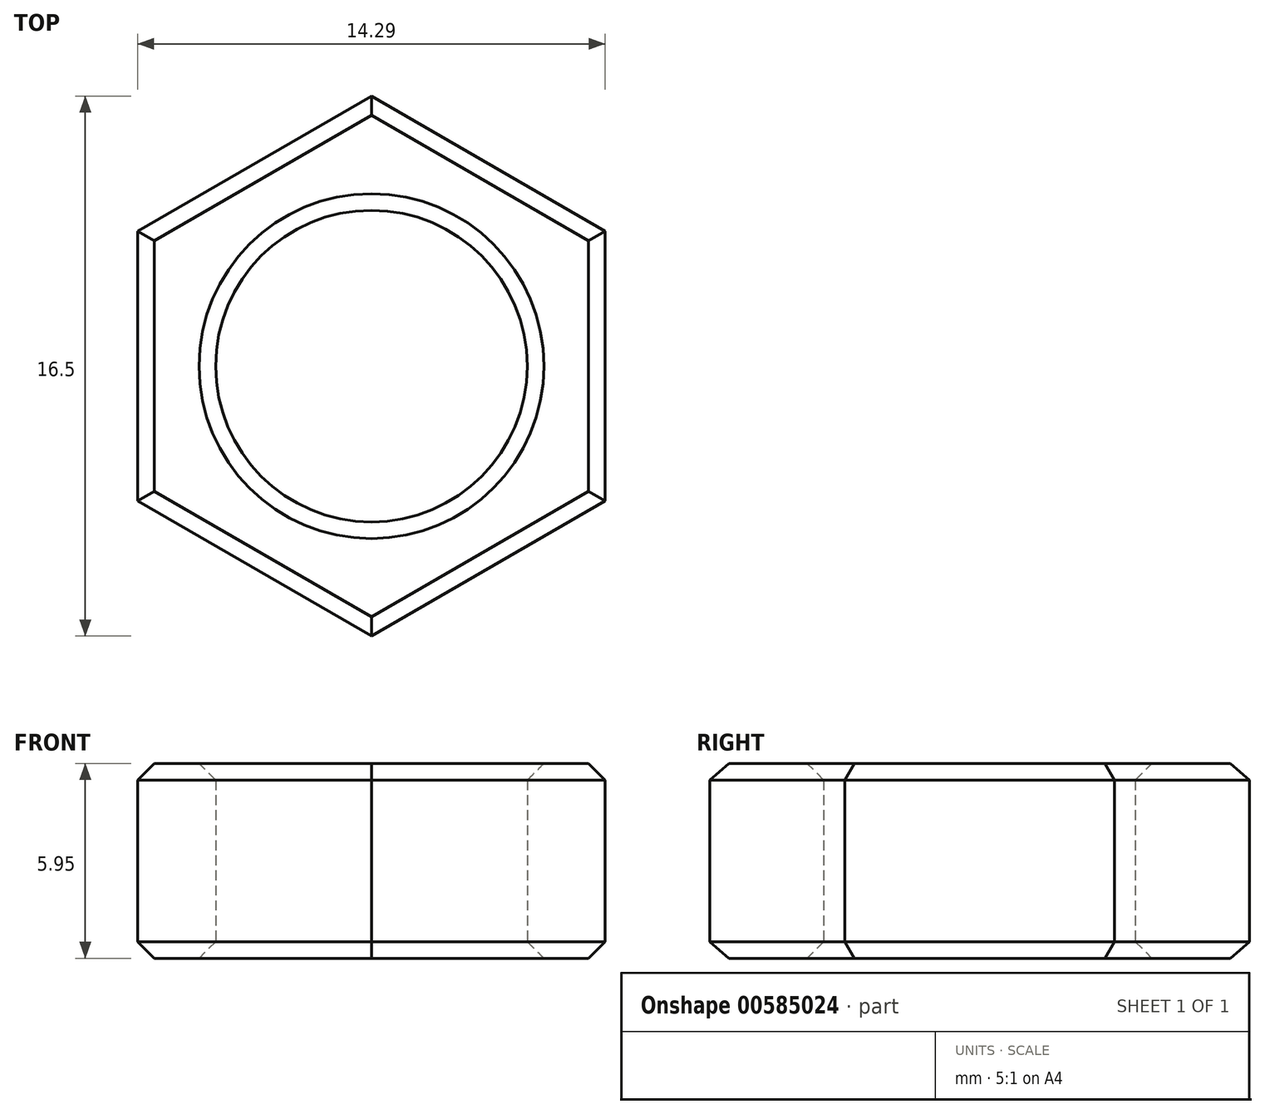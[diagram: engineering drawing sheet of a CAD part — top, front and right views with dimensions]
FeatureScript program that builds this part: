
annotation { "Feature Type Name" : "Feature", "Feature Type Description" : "" }
export const myFeature = defineFeature(function(context is Context, id is Id, definition is map)
    precondition{}
    {
        {
            var Q0;
            Q0=qCreatedBy(makeId("Top.planeOp"),FACE);
            var sketch = newSketch(context, id + "F0", { "sketchPlane" : qUnion([Q0])});
            skCircle(sketch, "E0.cCircle", {"center": v(-0.14, 0.22) * mm, "radius": 7.14 * mm, "construction": true});
            skLineSegment(sketch, "E0.0", {"start": v(7, 4.34) * mm, "end": v(7, -3.9) * mm});
            skLineSegment(sketch, "E0.1", {"start": v(7, -3.9) * mm, "end": v(-0.14, -8.03) * mm});
            skLineSegment(sketch, "E0.2", {"start": v(-0.14, -8.03) * mm, "end": v(-7.29, -3.9) * mm});
            skLineSegment(sketch, "E0.3", {"start": v(-7.29, -3.9) * mm, "end": v(-7.29, 4.34) * mm});
            skLineSegment(sketch, "E0.4", {"start": v(-7.29, 4.34) * mm, "end": v(-0.14, 8.47) * mm});
            skLineSegment(sketch, "E0.5", {"start": v(-0.14, 8.47) * mm, "end": v(7, 4.34) * mm});
            skPoint(sketch, "E0.0.midPoint", {"position": v(7, 0.22) * mm});
            skCircle(sketch, "E1", {"center": v(-0.14, 0.22) * mm, "radius": 4.76 * mm});
            skSolve(sketch);
        }
        {
            var Q0;
            Q0 = qSketchRegion(id + "F0", true);
            extrude(context, id + "F1", {"entities" : qUnion([Q0]), "depth" : 5.95 * mm, "offsetDistance" : 25.4 * mm});
        }
        {
            var Q0;
            Q0=makeQuery(id+"F1.opExtrude","CAP_EDGE",EDGE,{"disambiguationData":[OSD([sQuery(id+"F0.wireOp",EDGE,"E0.4")])],"isStart":false});
            var Q1;
            Q1=makeQuery(id+"F1.opExtrude","CAP_EDGE",EDGE,{"disambiguationData":[OSD([sQuery(id+"F0.wireOp",EDGE,"E0.5")])],"isStart":false});
            var Q2;
            Q2=makeQuery(id+"F1.opExtrude","CAP_EDGE",EDGE,{"disambiguationData":[OSD([sQuery(id+"F0.wireOp",EDGE,"E0.0")])],"isStart":false});
            var Q3;
            Q3=makeQuery(id+"F1.opExtrude","CAP_EDGE",EDGE,{"disambiguationData":[OSD([sQuery(id+"F0.wireOp",EDGE,"E0.1")])],"isStart":false});
            var Q4;
            Q4=makeQuery(id+"F1.opExtrude","CAP_EDGE",EDGE,{"disambiguationData":[OSD([sQuery(id+"F0.wireOp",EDGE,"E0.2")])],"isStart":false});
            var Q5;
            Q5=makeQuery(id+"F1.opExtrude","CAP_EDGE",EDGE,{"disambiguationData":[OSD([sQuery(id+"F0.wireOp",EDGE,"E0.3")])],"isStart":false});
            var Q6;
            Q6=makeQuery(id+"F1.opExtrude","CAP_EDGE",EDGE,{"disambiguationData":[OSD([sQuery(id+"F0.wireOp",EDGE,"E0.1")])],"isStart":true});
            var Q7;
            Q7=makeQuery(id+"F1.opExtrude","CAP_EDGE",EDGE,{"disambiguationData":[OSD([sQuery(id+"F0.wireOp",EDGE,"E0.0")])],"isStart":true});
            var Q8;
            Q8=makeQuery(id+"F1.opExtrude","CAP_EDGE",EDGE,{"disambiguationData":[OSD([sQuery(id+"F0.wireOp",EDGE,"E0.5")])],"isStart":true});
            var Q9;
            Q9=makeQuery(id+"F1.opExtrude","CAP_EDGE",EDGE,{"disambiguationData":[OSD([sQuery(id+"F0.wireOp",EDGE,"E0.4")])],"isStart":true});
            var Q10;
            Q10=makeQuery(id+"F1.opExtrude","CAP_EDGE",EDGE,{"disambiguationData":[OSD([sQuery(id+"F0.wireOp",EDGE,"E0.3")])],"isStart":true});
            var Q11;
            Q11=makeQuery(id+"F1.opExtrude","CAP_EDGE",EDGE,{"disambiguationData":[OSD([sQuery(id+"F0.wireOp",EDGE,"E0.2")])],"isStart":true});
            var Q12;
            Q12=makeQuery(id+"F1.opExtrude","CAP_EDGE",EDGE,{"disambiguationData":[OSD([sQuery(id+"F0.wireOp",EDGE,"E1")])],"isStart":false});
            var Q13;
            Q13=makeQuery(id+"F1.opExtrude","CAP_EDGE",EDGE,{"disambiguationData":[OSD([sQuery(id+"F0.wireOp",EDGE,"E1")])],"isStart":true});
            chamfer(context, id + "F2", {"entities" : qUnion([Q0, Q1, Q2, Q3, Q4, Q5, Q6, Q7, Q8, Q9, Q10, Q11, Q12, Q13]), "width" : 0.5 * mm, "tangentPropagation" : true});
        }
    });
